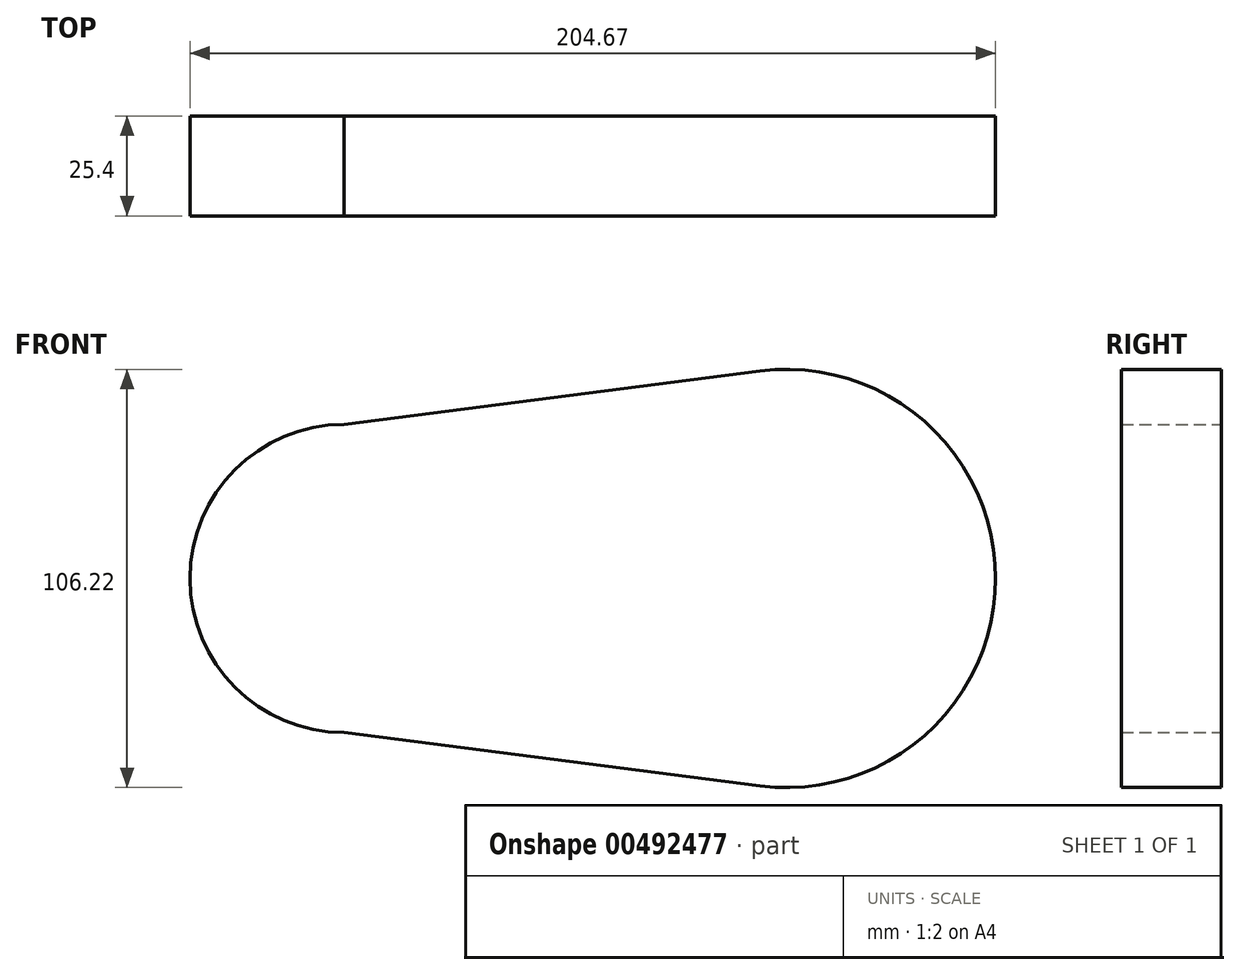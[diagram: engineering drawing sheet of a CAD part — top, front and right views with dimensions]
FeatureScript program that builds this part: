
annotation { "Feature Type Name" : "Feature", "Feature Type Description" : "" }
export const myFeature = defineFeature(function(context is Context, id is Id, definition is map)
    precondition{}
    {
        {
            var Q0;
            Q0=qCreatedBy(makeId("Front.planeOp"),FACE);
            var sketch = newSketch(context, id + "F0", { "sketchPlane" : qUnion([Q0])});
            skCircle(sketch, "E0", {"center": v(0, 0) * mm, "radius": 39.13 * mm});
            skCircle(sketch, "E1", {"center": v(112.43, 0) * mm, "radius": 53.11 * mm});
            skLineSegment(sketch, "E2", {"start": v(0, 39.13) * mm, "end": v(105.67, 52.68) * mm});
            skLineSegment(sketch, "E3", {"start": v(0, -39.13) * mm, "end": v(105.67, -52.68) * mm});
            skSolve(sketch);
        }
        {
            var Q0;
            Q0 = qSketchRegion(id + "F0", true);
            extrude(context, id + "F1", {"entities" : qUnion([Q0]), "depth" : 25.4 * mm});
        }
    });
